# Revit family: BISLEY_SystemFile_Tambours_Double
name_source: partatom
category: Furniture
revit_build: Autodesk Revit 2018 (Build: 20180423_1000(x64)
units: mm (PartAtom-declared; Revit-internal decimal feet)

## family parameters
Always vertical = Yes
Cut with Voids When Loaded = No
OmniClass Number = 23.40.20.00
OmniClass Title = General Furniture and Specialties
Room Calculation Point = No
Shared = No
Work Plane-Based = No

## types (16) — shared parameters
Category = Furniture
Compliance Standards Certification = BS EN 14073 2004 Part 2 & 3, BS EN 14074, BS 4875 1998 Part 7 level 4 & Part 8, BS 476 Part 7 1987 Class 2Y
Depth = 470 mm  [stored 1.54199 ft]
Description = Double Tambour
Finish = Powder Coated
Manufacturer = Bisley
Material = Steel
Plinth height = 55 mm  [stored 0.180446 ft]
Range = SystemFile
Routine Maintenance = We recommend you clean your unit with warm water and a mild detergent solution. A damp cloth can be used to remove dust particles.
Start door height = -35 mm  [stored -0.114829 ft]
URL = www.bisley.com
Uniclass 2015 Code = PR_40_30_57
Uniclass2015Title = Shelves and Storage Units
Uniclass2015Version = V1.1
Warranty = 10 years
plinth start height = -35 mm  [stored -0.114829 ft]

## per-type parameters (varying)
| type | Doors height | Height | Lock bar height | Tambour array | Width |
| SYT10/2 | 554 mm  [stored 1.81759 ft] | 693 mm  [stored 2.27362 ft] | 554 mm  [stored 1.81759 ft] | 15 | 1000 mm  [stored 3.28084 ft] |
| SYT10/3 | 858 mm | 997 mm | 858 mm | 15 | 1000 mm  [stored 3.28084 ft] |
| SYT10/34 | 1010 mm | 1149 mm  [stored 3.76969 ft] | 1010 mm | 15 | 1000 mm  [stored 3.28084 ft] |
| SYT10/4 | 1162 mm | 1301 mm  [stored 4.26837 ft] | 1162 mm | 15 | 1000 mm  [stored 3.28084 ft] |
| SYT10/43 | 1276 mm | 1415 mm  [stored 4.64239 ft] | 1276 mm | 15 | 1000 mm  [stored 3.28084 ft] |
| SYT10/50 | 1504 mm  [stored 4.93438 ft] | 1643 mm  [stored 5.39042 ft] | 1504 mm  [stored 4.93438 ft] | 15 | 1000 mm  [stored 3.28084 ft] |
| SYT10/54 | 1656 mm  [stored 5.43307 ft] | 1795 mm | 1656 mm  [stored 5.43307 ft] | 15 | 1000 mm  [stored 3.28084 ft] |
| SYT10/6 | 1808 mm  [stored 5.93176 ft] | 1947 mm  [stored 6.3878 ft] | 1808 mm  [stored 5.93176 ft] | 15 | 1000 mm  [stored 3.28084 ft] |
| SYT12/2 | 554 mm  [stored 1.81759 ft] | 693 mm  [stored 2.27362 ft] | 554 mm  [stored 1.81759 ft] | 18 | 1200 mm |
| SYT12/3 | 858 mm | 997 mm | 858 mm | 18 | 1200 mm |
| SYT12/34 | 1010 mm | 1149 mm  [stored 3.76969 ft] | 1010 mm | 18 | 1200 mm |
| SYT12/4 | 1162 mm | 1301 mm  [stored 4.26837 ft] | 1162 mm | 18 | 1200 mm |
| SYT12/43 | 1276 mm | 1415 mm  [stored 4.64239 ft] | 1276 mm | 18 | 1200 mm |
| SYT12/50 | 1504 mm  [stored 4.93438 ft] | 1643 mm  [stored 5.39042 ft] | 1504 mm  [stored 4.93438 ft] | 18 | 1200 mm |
| SYT12/54 | 1656 mm  [stored 5.43307 ft] | 1795 mm | 1656 mm  [stored 5.43307 ft] | 18 | 1200 mm |
| SYT12/6 | 1808 mm  [stored 5.93176 ft] | 1947 mm  [stored 6.3878 ft] | 1808 mm  [stored 5.93176 ft] | 18 | 1200 mm |

note: column(s) folded — value = type name in every type: Model Reference

note: [stored X ft] marks values corroborated as IEEE doubles in the binary element streams (Revit-internal decimal feet)

## geometry (parser evidence)
native form markers: Sweep x1
no freeform markers — native parametric forms only
